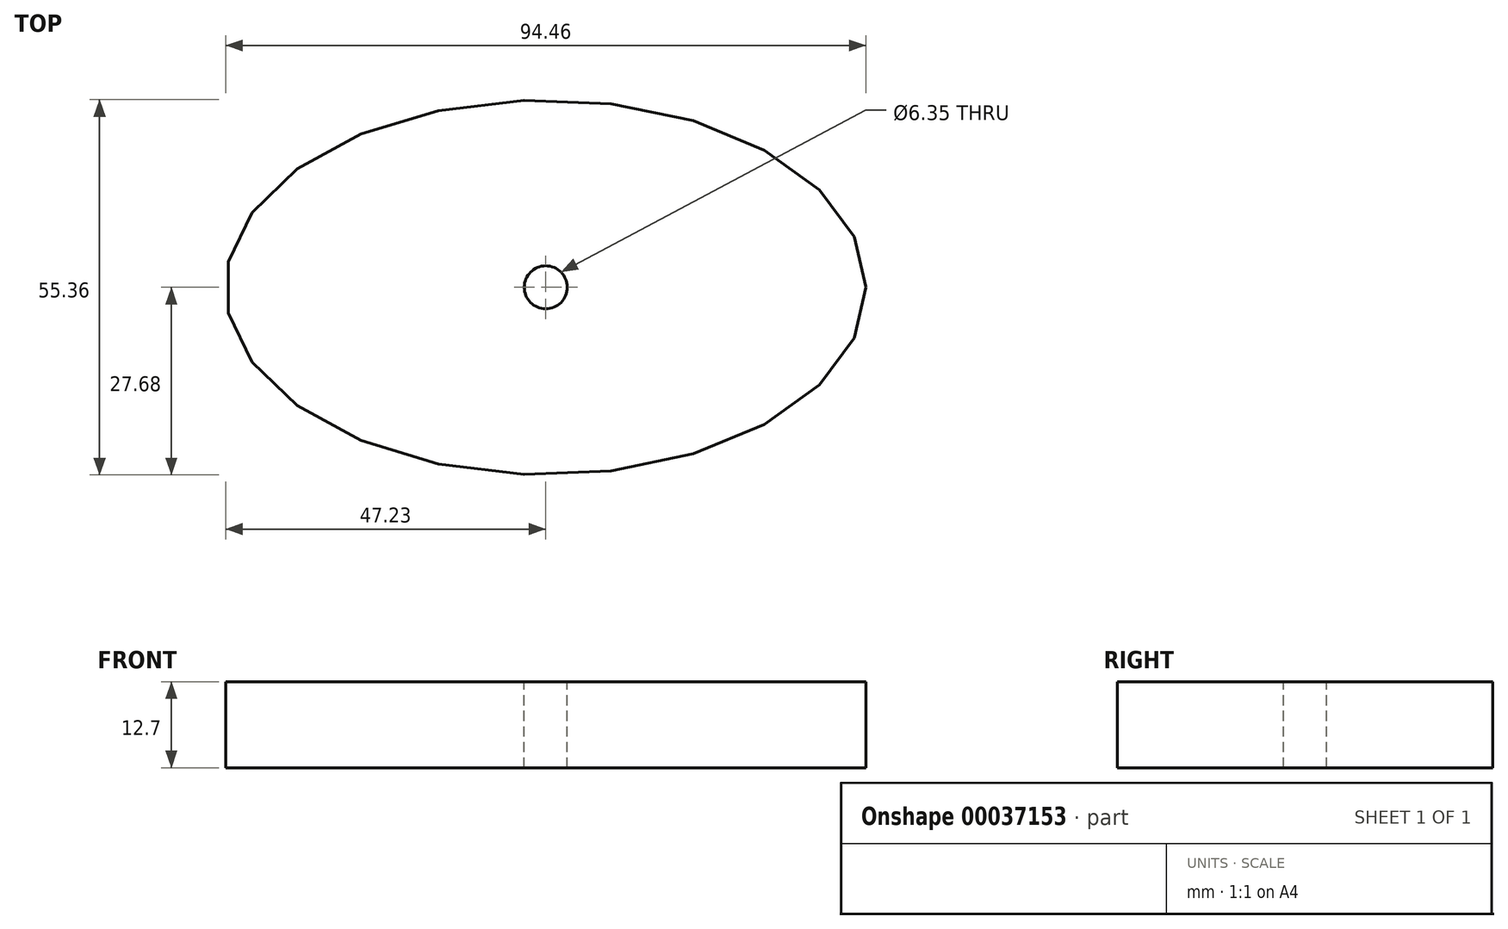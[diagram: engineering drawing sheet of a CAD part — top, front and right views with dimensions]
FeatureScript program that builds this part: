
annotation { "Feature Type Name" : "Feature", "Feature Type Description" : "" }
export const myFeature = defineFeature(function(context is Context, id is Id, definition is map)
    precondition{}
    {
        {
            var Q0;
            Q0=qCreatedBy(makeId("Top.planeOp"),FACE);
            var sketch = newSketch(context, id + "F0", { "sketchPlane" : qUnion([Q0])});
            skEllipse(sketch, "E0", {"center": v(0, 0) * mm, "majorRadius": 47.23 * mm, "minorRadius": 27.68 * mm, "majorAxis": v(1, 0)});
            skSolve(sketch);
        }
        {
            var Q0;
            Q0 = qSketchRegion(id + "F0", true);
            extrude(context, id + "F1", {"entities" : qUnion([Q0]), "depth" : 12.7 * mm});
        }
        {
            var Q0;
            Q0=makeQuery(id+"F1.opExtrude","CAP_FACE",FACE,{"disambiguationData":[OSD([sQuery(id+"F0.wireOp",EDGE,"E0")])],"isStart":false});
            var sketch = newSketch(context, id + "F2", { "sketchPlane" : qUnion([Q0])});
            skCircle(sketch, "E1", {"center": v(0, 0) * mm, "radius": 8.21 * mm});
            skSolve(sketch);
        }
        {
            var Q0;
            Q0=sQuery(id+"F2.wireOp",VERTEX,"E1.center");
            var Q1;
            Q1=makeQuery(id+"F1.opExtrude","SWEPT_BODY",BODY,{"disambiguationData":[OSD([sQuery(id+"F0.wireOp",EDGE,"E0")])]});
            hole(context, id + "F3", {"style" : HoleStyle.SIMPLE, "holeDiameter" : 6.35 * mm, "endStyle" : HoleEndStyle.THROUGH, "locations" : qUnion([Q0]), "scope" : qUnion([Q1])});
        }
    });
